# Revit family: Reece_Basin_LAUFEN_Kartell_Freestanding Basin
name_source: partatom
category: Plumbing Fixtures
revit_build: Autodesk Revit 2018 (Build: 20180329_1100(x64)
units: mm (PartAtom-declared; Revit-internal decimal feet)

## family parameters
Always vertical = Yes
Cut with Voids When Loaded = Yes
Part Type = Normal
Room Calculation Point = Yes
Round Connector Dimension = Use Diameter
Shared = Yes
Work Plane-Based = Yes

## types (1)
- 1 Taphole_Centre Bowl_375 mm_16.3 L_Vitreous China_White
    Default Elevation = 0 mm  [stored 0 ft]
    Description = LAUFEN Kartell Freestanding Basin / Pedestal with Overflow 375 x 435 x 900mm 1 Taphole White
    Disclaimer = THIS FILE IS THE PROPERTY OF THE REECE GROUP. IT MAY NOT BE REPRODUCED, REVERSE-ENGINEERED OR MODIFIED. ANY REPUBLICATION, TRANSMISSION OR DISTRIBUTION FOR THE PURPOSE OF COMMERCIALLY EXPLOITING THE FILES IS PROHIBITED.
    Keynote = Product #9504675, Reece_Basin_LAUFEN_Kartell_Freestanding Basin - 1 Taphole_Centre Bowl_375 mm_16.3 L_Vitreous China_White
    Manufacturer = LAUFEN
    Model = Kartell
    Reece_Basin_Outlet = 40 mm  [stored 0.131234 ft]
    Reece_Detail_Additional = Overflow
    Reece_Detail_Disclaimer = THIS FILE IS THE PROPERTY OF THE REECE GROUP. IT MAY NOT BE REPRODUCED, REVERSE-ENGINEERED OR MODIFIED. ANY REPUBLICATION, TRANSMISSION OR DISTRIBUTION FOR THE PURPOSE OF COMMERCIALLY EXPLOITING THE FILES IS PROHIBITED.
    Reece_Material_Main = Reece_Vitreous China_White
    Reece_Overall_Capacity = 16.3 L
    Reece_Overall_Height = 900 mm  [stored 2.95276 ft]
    Reece_Overall_Length = 435 mm  [stored 1.42717 ft]
    Reece_Overall_Width = 375 mm
    Reece_Product_Brand = LAUFEN
    Reece_Product_Description = LAUFEN Kartell Freestanding Basin/Pedestal with Overflow 375 x 435 x 900mm 1 Taphole White
    Reece_Product_Mount = Floor Mounted
    Reece_Product_Number = 9504675
    Reece_Product_Sub Brand = Kartell
    Reece_Product_Type = Basin
    Reece_Product_Web Page = https://www.reece.com.au
    Type Comments = Basin
    URL = https://www.reece.com.au

note: [stored X ft] marks values corroborated as IEEE doubles in the binary element streams (Revit-internal decimal feet)

## geometry (parser evidence)
native form markers: Sweep x2
no freeform markers — native parametric forms only
